# Revit family: JC KONTAKTER JCK107 Armbågskontakt
name_source: partatom
category: Specialty Equipment
units: mm (PartAtom-declared; Revit-internal decimal feet)

## family parameters
Always vertical = Yes
Cut with Voids When Loaded = No
Enable Cutting in Views = Yes
Host = Wall
Maintain Annotation Orientation = No
Part Type = Normal
Room Calculation Point = No
Round Connector Dimension = Use Diameter
Shared = No

## types (1)
- Armbågskontakt JCK107
    Antal mikrobrytare = 1
    CE Dokument = https://jckontakter.se
    Core Finish = ABS 750SW (Mörk grå)
    Default Elevation = 0 mm  [stored 0 ft]
    Description = JCK107 är en stilren armbågskontakt i tålig ABS-plast. Modell med plan tryckplatta i rostfri metall och mörkgrå underdel.
JCK107 levereras med 1st mikrobrytare i IP67, men går även att beställa med fler.
    Lid Finish = ABS 750SW (Silver färg)
    Lägsta märkström = 1mA/4 V DC
    Manufacturer = JC Kontakter
    Mikrobrytare = Standard NO IP67
    Model = JCK107
    Nominell märkström = 12 V - Resistive 6A Inductive L/R 5ms 6A, 24 V - Resistive 6A Inductive L/R 5ms 5A
    Placering av armbågskontakt = https://jckontakter.se
    Plate Finish = Stainless Steel EN 1.4301
    Produktvikt = 0.321 kg
    Tekniskt produktblad = https://jckontakter.se
    Tillvalsförteckning = https://jckontakter.se
    Tillverkningsland = Sverige
    URL = https://jckontakter.se

note: [stored X ft] marks values corroborated as IEEE doubles in the binary element streams (Revit-internal decimal feet)

## geometry (parser evidence)
native form markers: Sweep x7
no freeform markers — native parametric forms only
